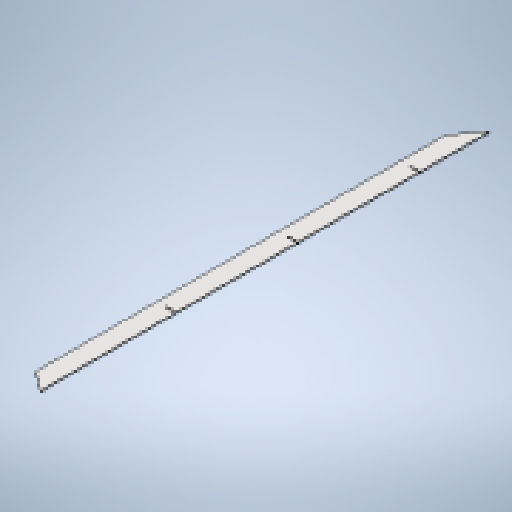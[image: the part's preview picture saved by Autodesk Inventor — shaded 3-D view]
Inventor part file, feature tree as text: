
AUTODESK INVENTOR PART (.ipt)
format: ipt  version: 2025 (Build 290162010, 162A)  size: 213,504 bytes
history: native  units: mm
features: other x4, chamfer x2, sketch x2, sheet_metal_op x1, extrude x1, pattern_linear x1
ambient origin geometry x8: Origin, YZ Plane, XZ Plane, XY Plane, X Axis, Y Axis, Z Axis, Center Point
bodies: Solid1 (feature_tree)
feature tree (11):
  sheet_metal_op  "Face1"
  other  "Corner Chamfer1"
  chamfer  "Corner Round1"
  chamfer  "Corner Round2"
  other  "Corner Chamfer3"
  extrude  "Extrusion1"  Depth=50.0mm
  pattern_linear  "Rectangular Pattern1"  Spacing1=9.372418mm  [1 undecoded]
  sketch  "Sketch1"  dims[d0=50.0mm d1=1190.0mm]
  other  "Plate1"
  sketch  "Sketch3"  dims[d2=3.0mm d5=9.372418mm d6=9.372418mm d7=3.0mm d8=6.0mm d9=45.0deg d13=6.0mm d14=6.0mm d15=3.0mm d16=6.0mm d17=45.0deg d18=187.0mm d19=26.0mm d20=3.0mm d21=0.0mm d22=0.0mm d23=30.0mm d25=323.0mm]
  other  "Definition1"
note: 1 required parameter value undecoded (feature->parameter linkage not recoverable at this tier; creation-order binding heuristic only, values carry confidence <= 0.55)
